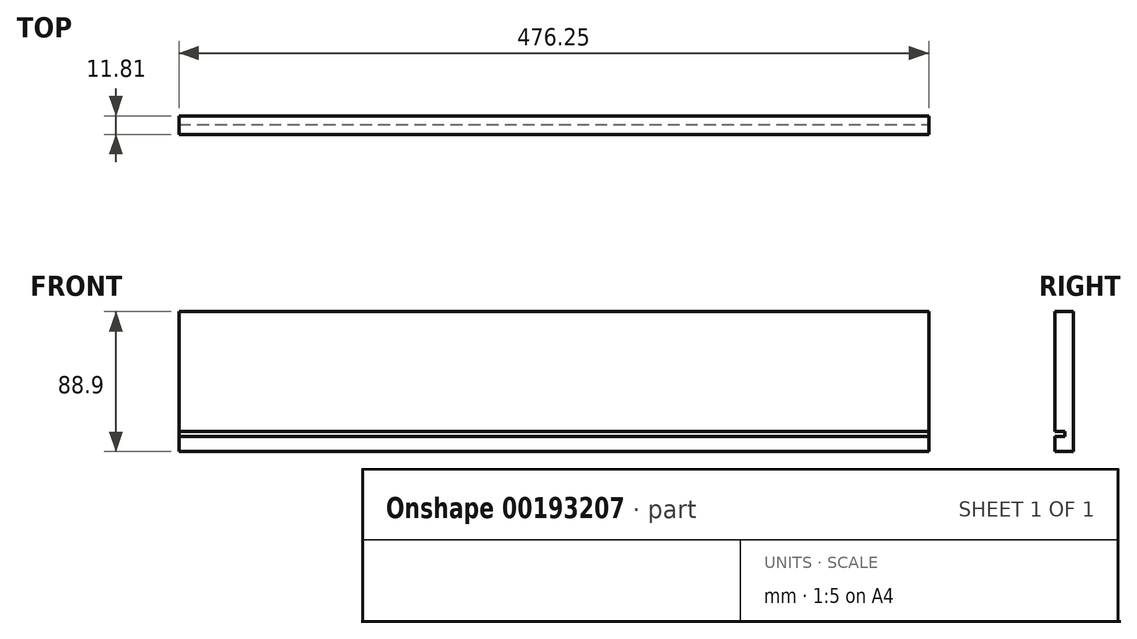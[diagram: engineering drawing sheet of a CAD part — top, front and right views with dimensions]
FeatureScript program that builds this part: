
annotation { "Feature Type Name" : "Feature", "Feature Type Description" : "" }
export const myFeature = defineFeature(function(context is Context, id is Id, definition is map)
    precondition{}
    {
        {
            var Q0;
            Q0=qCreatedBy(makeId("Right.planeOp"),FACE);
            var sketch = newSketch(context, id + "F0", { "sketchPlane" : qUnion([Q0])});
            skLineSegment(sketch, "E0.bottom", {"start": v(0, 0) * mm, "end": v(11.81, 0) * mm});
            skLineSegment(sketch, "E0.top", {"start": v(0, -88.9) * mm, "end": v(11.81, -88.9) * mm});
            skLineSegment(sketch, "E0.left", {"start": v(0, 0) * mm, "end": v(0, -76.2) * mm});
            skLineSegment(sketch, "E0.right", {"start": v(11.81, 0) * mm, "end": v(11.81, -88.9) * mm});
            skLineSegment(sketch, "E1.bottom", {"start": v(0, -76.2) * mm, "end": v(6.35, -76.2) * mm});
            skLineSegment(sketch, "E1.top", {"start": v(0, -79.38) * mm, "end": v(6.35, -79.38) * mm});
            skLineSegment(sketch, "E1.right", {"start": v(6.35, -76.2) * mm, "end": v(6.35, -79.38) * mm});
            skLineSegment(sketch, "E2.trimOffspring", {"start": v(0, -79.38) * mm, "end": v(0, -88.9) * mm});
            skSolve(sketch);
        }
        {
            var Q0;
            Q0 = qSketchRegion(id + "F0", true);
            var Q1;
            Q1 = qConstructionFilter(qBodyType(qCreatedBy(id + "F0" ,EDGE), BodyType.WIRE), ConstructionObject.NO);
            extrude(context, id + "F1", {"entities" : qUnion([Q0]), "surfaceEntities" : qUnion([Q1]), "oppositeDirection" : true, "depth" : 476.25 * mm});
        }
    });
